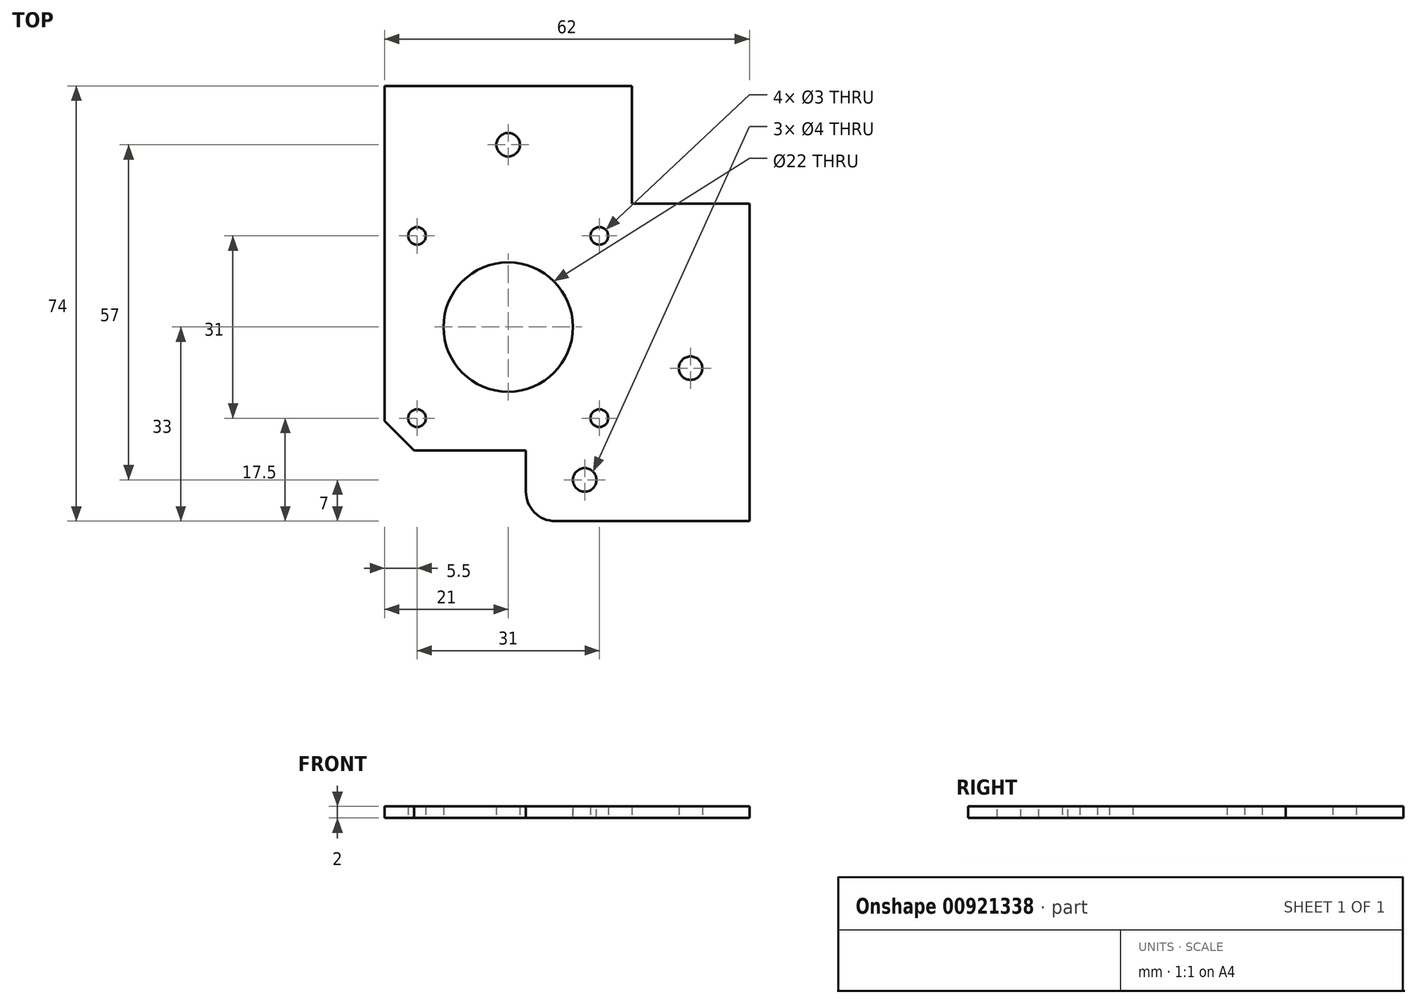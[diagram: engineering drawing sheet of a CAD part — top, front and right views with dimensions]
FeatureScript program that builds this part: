
annotation { "Feature Type Name" : "Feature", "Feature Type Description" : "" }
export const myFeature = defineFeature(function(context is Context, id is Id, definition is map)
    precondition{}
    {
        {
            var Q0;
            Q0=qCreatedBy(makeId("Top.planeOp"),FACE);
            var sketch = newSketch(context, id + "F0", { "sketchPlane" : qUnion([Q0])});
            skLineSegment(sketch, "E0.bottom", {"start": v(31, -31) * mm, "end": v(-31, -31) * mm});
            skLineSegment(sketch, "E0.top", {"start": v(31, 31) * mm, "end": v(-31, 31) * mm});
            skLineSegment(sketch, "E0.left", {"start": v(31, -31) * mm, "end": v(31, 31) * mm});
            skLineSegment(sketch, "E0.right", {"start": v(-31, -31) * mm, "end": v(-31, 31) * mm});
            skPoint(sketch, "E0.middle", {"position": v(0, 0) * mm});
            skLineSegment(sketch, "E1.bottom", {"start": v(31, 31) * mm, "end": v(11, 31) * mm});
            skLineSegment(sketch, "E1.top", {"start": v(31, 11) * mm, "end": v(11, 11) * mm});
            skLineSegment(sketch, "E1.left", {"start": v(31, 31) * mm, "end": v(31, 11) * mm});
            skLineSegment(sketch, "E1.right", {"start": v(11, 31) * mm, "end": v(11, 11) * mm});
            skCircle(sketch, "E2", {"center": v(-10, -10) * mm, "radius": 11 * mm});
            skCircle(sketch, "E3", {"center": v(-25.5, 5.5) * mm, "radius": 1.5 * mm});
            skCircle(sketch, "E4", {"center": v(-25.5, -25.5) * mm, "radius": 1.5 * mm});
            skCircle(sketch, "E5", {"center": v(5.5, -25.5) * mm, "radius": 1.5 * mm});
            skCircle(sketch, "E6", {"center": v(5.5, 5.5) * mm, "radius": 1.5 * mm});
            skCircle(sketch, "E7", {"center": v(-10, 21) * mm, "radius": 2 * mm});
            skCircle(sketch, "E8", {"center": v(21, -17) * mm, "radius": 2 * mm});
            skSolve(sketch);
        }
        {
            var Q0;
            Q0=makeQuery(id+"F0.imprint","IMPRINT",FACE,{"disambiguationData":[TD([[makeQuery(id+"F0.imprint","IMPRINT",EDGE,{"derivedFrom":sQuery(id+"F0.wireOp",EDGE,"E0.bottom")}),-1.0]])]});
            extrude(context, id + "F1", {"entities" : qUnion([Q0]), "depth" : 2 * mm, "offsetDistance" : 25 * mm});
        }
        {
            var Q0;
            Q0=makeQuery(id+"F1.opExtrude","SWEPT_EDGE",EDGE,{"disambiguationData":[OSD([sQuery(id+"F0.wireOp",EDGE,"E0.bottom"),sQuery(id+"F0.wireOp",EDGE,"E0.right")])]});
            chamfer(context, id + "F2", {"entities" : qUnion([Q0]), "width" : 5 * mm, "tangentPropagation" : true});
        }
        {
            var Q0;
            Q0=makeQuery(id+"F1.opExtrude","CAP_FACE",FACE,{"disambiguationData":[OSD([sQuery(id+"F0.wireOp",EDGE,"E0.bottom"),sQuery(id+"F0.wireOp",EDGE,"E0.top"),sQuery(id+"F0.wireOp",EDGE,"E0.left"),sQuery(id+"F0.wireOp",EDGE,"E0.right"),sQuery(id+"F0.wireOp",EDGE,"E1.top"),sQuery(id+"F0.wireOp",EDGE,"E1.right"),sQuery(id+"F0.wireOp",EDGE,"E2"),sQuery(id+"F0.wireOp",EDGE,"E3"),sQuery(id+"F0.wireOp",EDGE,"E4"),sQuery(id+"F0.wireOp",EDGE,"E5"),sQuery(id+"F0.wireOp",EDGE,"E6"),sQuery(id+"F0.wireOp",EDGE,"E7"),sQuery(id+"F0.wireOp",EDGE,"E8")])],"isStart":false});
            var sketch = newSketch(context, id + "F3", { "sketchPlane" : qUnion([Q0])});
            skLineSegment(sketch, "E9.bottom", {"start": v(31, -31) * mm, "end": v(-7, -31) * mm});
            skLineSegment(sketch, "E9.top", {"start": v(31, -43) * mm, "end": v(-7, -43) * mm});
            skLineSegment(sketch, "E9.left", {"start": v(31, -31) * mm, "end": v(31, -43) * mm});
            skLineSegment(sketch, "E9.right", {"start": v(-7, -31) * mm, "end": v(-7, -43) * mm});
            skSolve(sketch);
        }
        {
            var Q0;
            Q0=makeQuery(id+"F3.imprint","IMPRINT",FACE,{"disambiguationData":[TD([[makeQuery(id+"F3.imprint","IMPRINT",EDGE,{"derivedFrom":sQuery(id+"F3.wireOp",EDGE,"E9.bottom")}),1.0]])]});
            extrude(context, id + "F4", {"entities" : qUnion([Q0]), "operationType" : NewBodyOperationType.ADD, "oppositeDirection" : true, "depth" : 2 * mm, "offsetDistance" : 25 * mm});
        }
        {
            var Q0;
            Q0=makeQuery(id+"F4.boolean.opBoolean","MERGE",FACE,{"derivedFrom":[makeQuery(id+"F1.opExtrude","CAP_FACE",FACE,{"disambiguationData":[OSD([sQuery(id+"F0.wireOp",EDGE,"E0.bottom"),sQuery(id+"F0.wireOp",EDGE,"E0.top"),sQuery(id+"F0.wireOp",EDGE,"E0.left"),sQuery(id+"F0.wireOp",EDGE,"E0.right"),sQuery(id+"F0.wireOp",EDGE,"E1.top"),sQuery(id+"F0.wireOp",EDGE,"E1.right"),sQuery(id+"F0.wireOp",EDGE,"E2"),sQuery(id+"F0.wireOp",EDGE,"E3"),sQuery(id+"F0.wireOp",EDGE,"E4"),sQuery(id+"F0.wireOp",EDGE,"E5"),sQuery(id+"F0.wireOp",EDGE,"E6"),sQuery(id+"F0.wireOp",EDGE,"E7"),sQuery(id+"F0.wireOp",EDGE,"E8")])],"isStart":false}),makeQuery(id+"F4.opExtrude","CAP_FACE",FACE,{"disambiguationData":[OSD([sQuery(id+"F3.wireOp",EDGE,"E9.bottom"),sQuery(id+"F3.wireOp",EDGE,"E9.top"),sQuery(id+"F3.wireOp",EDGE,"E9.left"),sQuery(id+"F3.wireOp",EDGE,"E9.right")])],"isStart":true})]});
            var sketch = newSketch(context, id + "F5", { "sketchPlane" : qUnion([Q0])});
            skCircle(sketch, "E10", {"center": v(3, -36) * mm, "radius": 2 * mm});
            skSolve(sketch);
        }
        {
            var Q0;
            Q0=makeQuery(id+"F5.imprint","IMPRINT",FACE,{"disambiguationData":[TD([[makeQuery(id+"F5.imprint","IMPRINT",EDGE,{"derivedFrom":sQuery(id+"F5.wireOp",EDGE,"E10")}),1.0]])]});
            extrude(context, id + "F6", {"entities" : qUnion([Q0]), "operationType" : NewBodyOperationType.REMOVE, "oppositeDirection" : true, "depth" : 25 * mm, "offsetDistance" : 25 * mm});
        }
        {
            var Q0;
            Q0=makeQuery(id+"F4.opExtrude","SWEPT_EDGE",EDGE,{"disambiguationData":[OSD([sQuery(id+"F3.wireOp",EDGE,"E9.top"),sQuery(id+"F3.wireOp",EDGE,"E9.right")])]});
            var Q1;
            Q1=makeQuery(id+"F4.opExtrude","SWEPT_EDGE",EDGE,{"disambiguationData":[OSD([sQuery(id+"F0.wireOp",EDGE,"E0.bottom"),sQuery(id+"F3.wireOp",EDGE,"E9.bottom"),sQuery(id+"F3.wireOp",EDGE,"E9.right")])]});
            fillet(context, id + "F7", {"entities" : qUnion([Q0, Q1]), "radius" : 5 * mm, "tangentPropagation" : true, "allowEdgeOverflow" : false});
        }
    });
